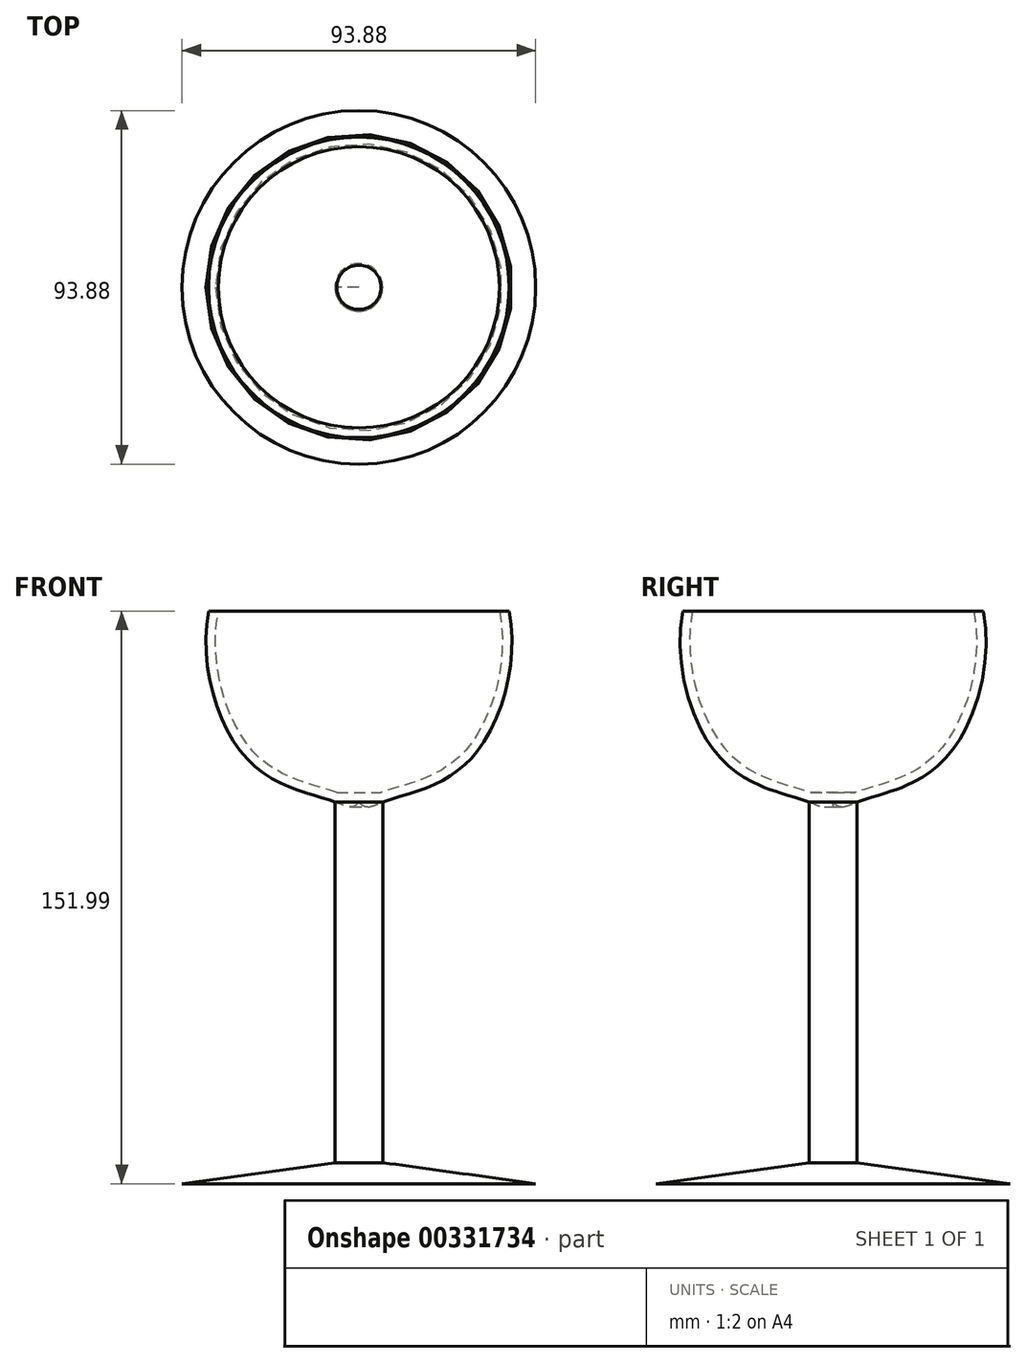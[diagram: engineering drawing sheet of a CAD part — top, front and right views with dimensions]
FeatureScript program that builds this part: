
annotation { "Feature Type Name" : "Feature", "Feature Type Description" : "" }
export const myFeature = defineFeature(function(context is Context, id is Id, definition is map)
    precondition{}
    {
        {
            var Q0;
            Q0=qCreatedBy(makeId("Front.planeOp"),FACE);
            var sketch = newSketch(context, id + "F0", { "sketchPlane" : qUnion([Q0])});
            skLineSegment(sketch, "E0", {"start": v(0, 75.25) * mm, "end": v(0, -76.74) * mm, "construction": true});
            skLineSegment(sketch, "E1", {"start": v(0, -76.74) * mm, "end": v(-46.94, -76.74) * mm});
            skLineSegment(sketch, "E2", {"start": v(-46.94, -76.74) * mm, "end": v(-6.33, -71.15) * mm});
            skLineSegment(sketch, "E3", {"start": v(-6.33, -71.15) * mm, "end": v(-6.33, 24.59) * mm});
            skLineSegment(sketch, "E4", {"start": v(-6.33, 24.59) * mm, "end": v(0, 24.59) * mm});
            skLineSegment(sketch, "E5", {"start": v(0, 24.59) * mm, "end": v(0, -76.74) * mm});
            skFitSpline(sketch, "E6", {"points": [v(-6.33, 24.59) * mm, v(-29.8, 36.13) * mm, v(-35.39, 87.17) * mm, v(0, 95.73) * mm, v(0, 24.59) * mm, v(-6.33, 24.59) * mm]});
            skLineSegment(sketch, "E7", {"start": v(0, 24.59) * mm, "end": v(0, 75.25) * mm});
            skLineSegment(sketch, "E8", {"start": v(0, 75.25) * mm, "end": v(-39.9, 75.25) * mm});
            skSolve(sketch);
        }
        {
            var Q0;
            Q0=makeQuery(id+"F0.imprint","IMPRINT",FACE,{"disambiguationData":[TD([[makeQuery(id+"F0.imprint","IMPRINT",EDGE,{"derivedFrom":sQuery(id+"F0.wireOp",EDGE,"E1")}),-1.0]])]});
            var Q1;
            Q1=sQuery(id+"F0.wireOp",EDGE,"E5");
            revolve(context, id + "F1", {"entities" : qUnion([Q0]), "axis" : qUnion([Q1]), "revolveType" : RevolveType.FULL});
        }
        {
            var Q0;
            Q0=makeQuery(id+"F0.imprint","IMPRINT",FACE,{"disambiguationData":[TD([[makeQuery(id+"F0.imprint","IMPRINT",EDGE,{"derivedFrom":sQuery(id+"F0.wireOp",EDGE,"E4")}),1.0]])]});
            var Q1;
            Q1=sQuery(id+"F0.wireOp",EDGE,"E7");
            revolve(context, id + "F2", {"operationType" : NewBodyOperationType.ADD, "entities" : qUnion([Q0]), "axis" : qUnion([Q1]), "revolveType" : RevolveType.FULL});
        }
        {
            var Q0;
            Q0=makeQuery(id+"F2.opRevolve","SWEPT_FACE",FACE,{"disambiguationData":[OSD([sQuery(id+"F0.wireOp",EDGE,"E8")])]});
            shell(context, id + "F3", {"entities" : qUnion([Q0]), "thickness" : 2.54 * mm});
        }
    });
